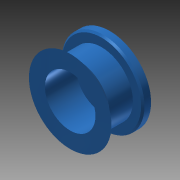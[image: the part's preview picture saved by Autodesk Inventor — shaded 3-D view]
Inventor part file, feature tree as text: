
AUTODESK INVENTOR PART (.ipt)
format: ipt  version: 2013 SP2 (Build 170200200, 200)  size: 116,736 bytes
history: native  units: mm
features: revolve x1, sketch x1
ambient origin geometry x8: Origin, YZ Plane, XZ Plane, XY Plane, X Axis, Y Axis, Z Axis, Center Point
bodies: Solid1 (feature_tree)
feature tree (2):
  revolve  "Revolution1"  [1 undecoded]
  sketch  "Sketch1"  dims[d6=12.0mm d7=7.65mm d10=90.0deg d17=7.0mm d18=2.5mm d19=135.0deg d20=3.0mm d21=2.0mm d22=2.5mm d23=12.5mm]
note: 1 required parameter value undecoded (feature->parameter linkage not recoverable at this tier; creation-order binding heuristic only, values carry confidence <= 0.55)
